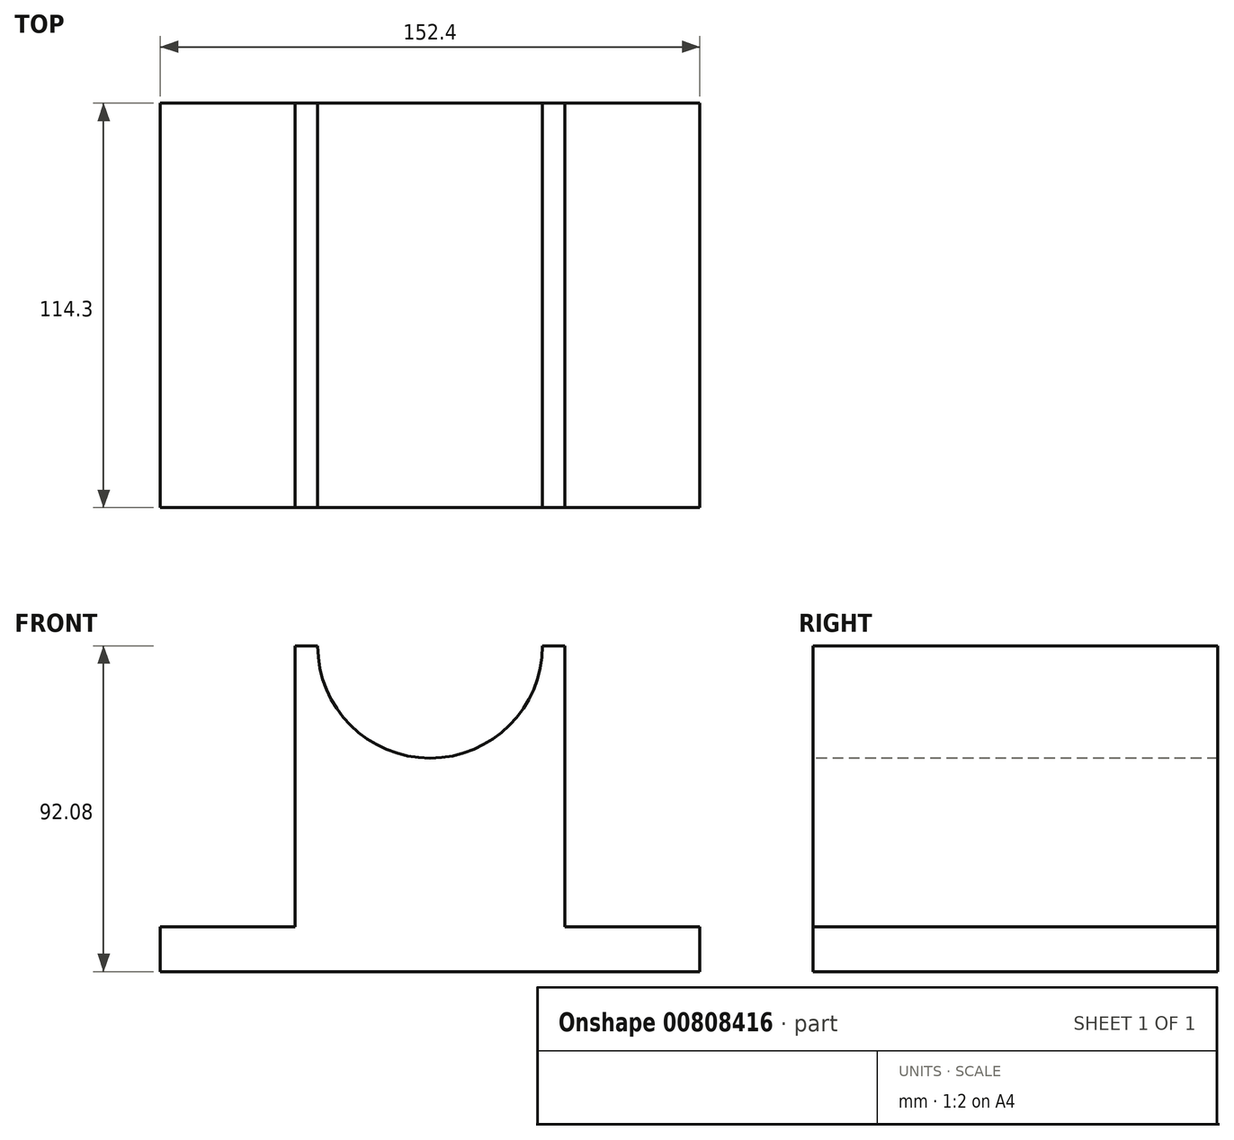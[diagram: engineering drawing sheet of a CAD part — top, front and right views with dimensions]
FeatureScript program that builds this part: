
annotation { "Feature Type Name" : "Feature", "Feature Type Description" : "" }
export const myFeature = defineFeature(function(context is Context, id is Id, definition is map)
    precondition{}
    {
        {
            var Q0;
            Q0=qCreatedBy(makeId("Front.planeOp"),FACE);
            var sketch = newSketch(context, id + "F0", { "sketchPlane" : qUnion([Q0])});
            skLineSegment(sketch, "E0", {"start": v(0, 0) * mm, "end": v(-152.4, 0) * mm});
            skLineSegment(sketch, "E1", {"start": v(0, 0) * mm, "end": v(0, 12.7) * mm});
            skLineSegment(sketch, "E2", {"start": v(0, 12.7) * mm, "end": v(-38.1, 12.7) * mm});
            skLineSegment(sketch, "E3", {"start": v(-38.1, 12.7) * mm, "end": v(-38.1, 92.08) * mm});
            skLineSegment(sketch, "E4", {"start": v(-38.1, 92.08) * mm, "end": v(-114.3, 92.08) * mm});
            skLineSegment(sketch, "E5", {"start": v(-114.3, 92.08) * mm, "end": v(-114.3, 12.7) * mm});
            skLineSegment(sketch, "E6", {"start": v(-114.3, 12.7) * mm, "end": v(-152.4, 12.7) * mm});
            skLineSegment(sketch, "E7", {"start": v(-152.4, 12.7) * mm, "end": v(-152.4, 0) * mm});
            skSolve(sketch);
        }
        {
            var Q0;
            Q0 = qSketchRegion(id + "F0", true);
            extrude(context, id + "F1", {"entities" : qUnion([Q0]), "depth" : 114.3 * mm, "offsetDistance" : 25.4 * mm});
        }
        {
            var Q0;
            Q0=makeQuery(id+"F1.opExtrude","CAP_FACE",FACE,{"disambiguationData":[OSD([sQuery(id+"F0.wireOp",EDGE,"E0"),sQuery(id+"F0.wireOp",EDGE,"E1"),sQuery(id+"F0.wireOp",EDGE,"E2"),sQuery(id+"F0.wireOp",EDGE,"E3"),sQuery(id+"F0.wireOp",EDGE,"E4"),sQuery(id+"F0.wireOp",EDGE,"E5"),sQuery(id+"F0.wireOp",EDGE,"E6"),sQuery(id+"F0.wireOp",EDGE,"E7")])],"isStart":false});
            var sketch = newSketch(context, id + "F2", { "sketchPlane" : qUnion([Q0])});
            skCircle(sketch, "E8", {"center": v(-76.2, 92.08) * mm, "radius": 31.75 * mm});
            skSolve(sketch);
        }
        {
            var Q0;
            Q0 = qSketchRegion(id + "F2", true);
            extrude(context, id + "F3", {"entities" : qUnion([Q0]), "operationType" : NewBodyOperationType.REMOVE, "oppositeDirection" : true, "depth" : 253974.6 * mm, "offsetDistance" : 25.4 * mm});
        }
    });
